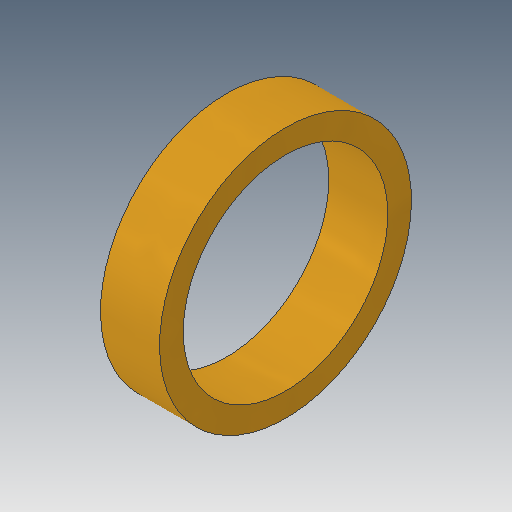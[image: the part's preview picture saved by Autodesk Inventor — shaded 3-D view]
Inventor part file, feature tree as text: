
AUTODESK INVENTOR PART (.ipt)
format: ipt  version: 2019.4 (Build 234330000, 330)  size: 100,864 bytes
history: native  units: mm
features: other x1, extrude x1, sketch x1
ambient origin geometry x8: Origin, YZ Plane, XZ Plane, XY Plane, X Axis, Y Axis, Z Axis, Center Point
bodies: Body1 (feature_tree)
feature tree (3):
  other  "ソリッド1"
  extrude  "押し出し1"  Depth=5.2mm
  sketch  "スケッチ1"
